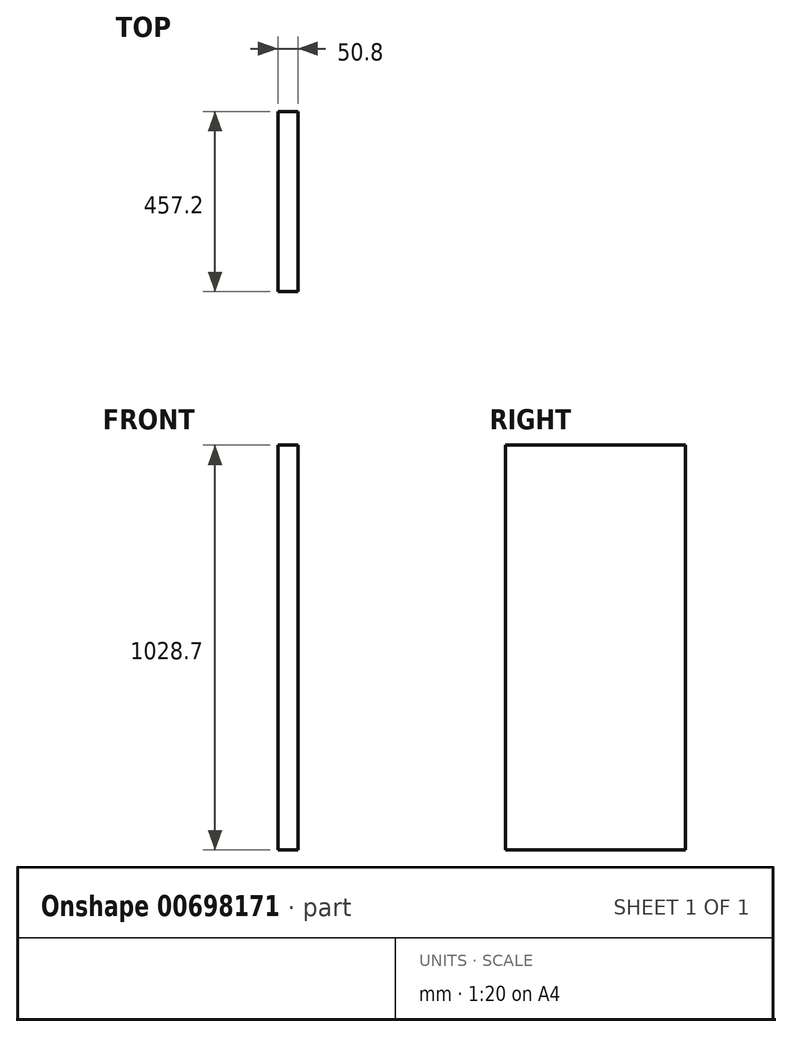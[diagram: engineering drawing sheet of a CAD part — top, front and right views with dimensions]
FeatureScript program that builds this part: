
annotation { "Feature Type Name" : "Feature", "Feature Type Description" : "" }
export const myFeature = defineFeature(function(context is Context, id is Id, definition is map)
    precondition{}
    {
        {
            var Q0;
            Q0=qCreatedBy(makeId("Right.planeOp"),FACE);
            var sketch = newSketch(context, id + "F0", { "sketchPlane" : qUnion([Q0])});
            skLineSegment(sketch, "E0.bottom", {"start": v(228.6, 514.35) * mm, "end": v(-228.6, 514.35) * mm});
            skLineSegment(sketch, "E0.top", {"start": v(228.6, -514.35) * mm, "end": v(-228.6, -514.35) * mm});
            skLineSegment(sketch, "E0.left", {"start": v(228.6, 514.35) * mm, "end": v(228.6, -514.35) * mm});
            skLineSegment(sketch, "E0.right", {"start": v(-228.6, 514.35) * mm, "end": v(-228.6, -514.35) * mm});
            skPoint(sketch, "E0.middle", {"position": v(0, 0) * mm});
            skSolve(sketch);
        }
        {
            var Q0;
            Q0=makeQuery(id+"F0.imprint","IMPRINT",FACE,{"disambiguationData":[TD([[makeQuery(id+"F0.imprint","IMPRINT",EDGE,{"derivedFrom":sQuery(id+"F0.wireOp",EDGE,"E0.bottom")}),1.0]])]});
            extrude(context, id + "F1", {"entities" : qUnion([Q0]), "depth" : 50.8 * mm, "offsetDistance" : 25.4 * mm});
        }
    });
